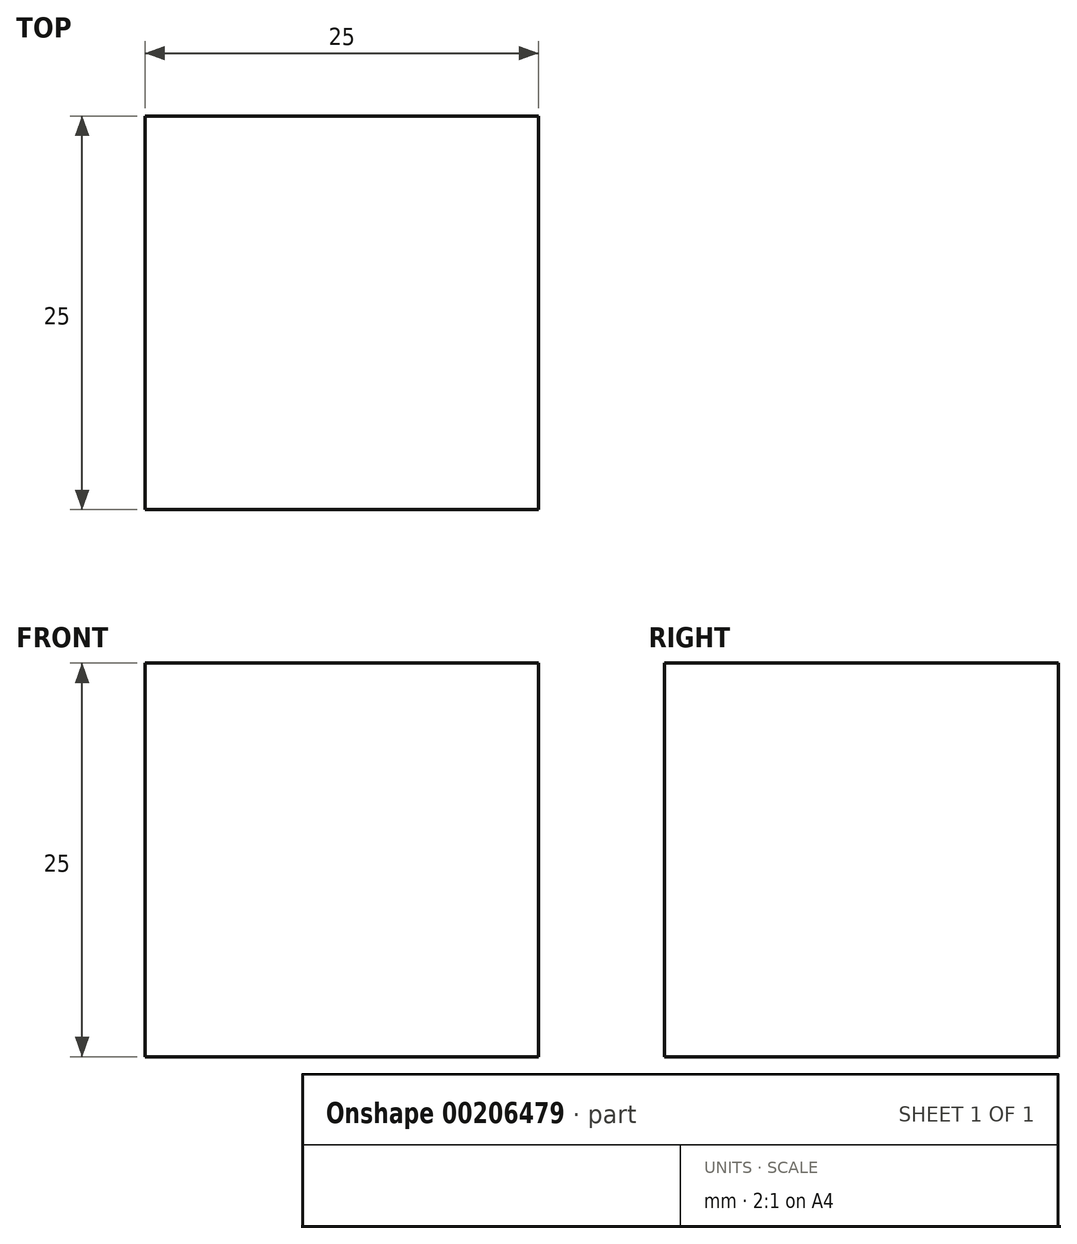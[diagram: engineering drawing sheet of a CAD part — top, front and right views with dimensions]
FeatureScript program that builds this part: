
annotation { "Feature Type Name" : "Feature", "Feature Type Description" : "" }
export const myFeature = defineFeature(function(context is Context, id is Id, definition is map)
    precondition{}
    {
        {
            var Q0;
            Q0=qCreatedBy(makeId("Top.planeOp"),FACE);
            var sketch = newSketch(context, id + "F0", { "sketchPlane" : qUnion([Q0])});
            skLineSegment(sketch, "E0.bottom", {"start": v(0, 0) * mm, "end": v(25, 0) * mm});
            skLineSegment(sketch, "E0.top", {"start": v(0, 25) * mm, "end": v(25, 25) * mm});
            skLineSegment(sketch, "E0.left", {"start": v(0, 0) * mm, "end": v(0, 25) * mm});
            skLineSegment(sketch, "E0.right", {"start": v(25, 0) * mm, "end": v(25, 25) * mm});
            skSolve(sketch);
        }
        {
            var Q0;
            Q0 = qSketchRegion(id + "F0", true);
            extrude(context, id + "F1", {"entities" : qUnion([Q0]), "depth" : 25 * mm, "offsetDistance" : 25 * mm});
        }
    });
